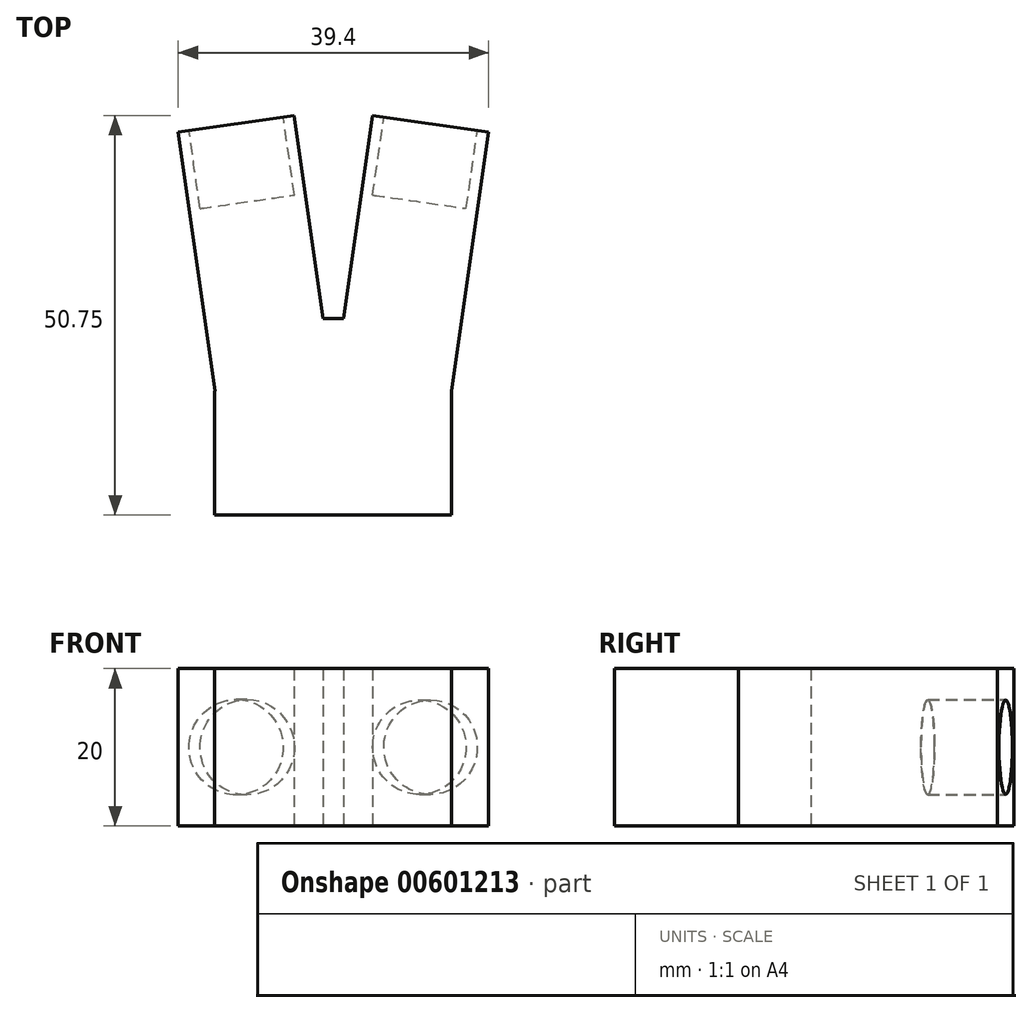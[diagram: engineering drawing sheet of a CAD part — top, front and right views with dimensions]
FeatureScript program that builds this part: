
annotation { "Feature Type Name" : "Feature", "Feature Type Description" : "" }
export const myFeature = defineFeature(function(context is Context, id is Id, definition is map)
    precondition{}
    {
        {
            var Q0;
            Q0=qCreatedBy(makeId("Top.planeOp"),FACE);
            var sketch = newSketch(context, id + "F0", { "sketchPlane" : qUnion([Q0])});
            skPoint(sketch, "E0.middle", {"position": v(0, 0) * mm});
            skLineSegment(sketch, "E1", {"start": v(-19.7, 32.9) * mm, "end": v(-15, 0) * mm});
            skLineSegment(sketch, "E2", {"start": v(19.7, 32.9) * mm, "end": v(15, 0) * mm});
            skPoint(sketch, "E3", {"position": v(-5, 35) * mm});
            skPoint(sketch, "E4", {"position": v(5, 35) * mm});
            skLineSegment(sketch, "E5", {"start": v(-1.32, 9.22) * mm, "end": v(-5, 35) * mm});
            skLineSegment(sketch, "E6", {"start": v(1.32, 9.22) * mm, "end": v(5, 35) * mm});
            skLineSegment(sketch, "E7", {"start": v(-1.32, 9.22) * mm, "end": v(1.32, 9.22) * mm});
            skPoint(sketch, "E8.start.orphan", {"position": v(16.32, 9.22) * mm});
            skPoint(sketch, "E9.orphan", {"position": v(-20, -35) * mm});
            skPoint(sketch, "E10.orphan", {"position": v(20, -35) * mm});
            skPoint(sketch, "E0.top.end.orphan", {"position": v(-10, -35) * mm});
            skPoint(sketch, "E11.orphan", {"position": v(10, -35) * mm});
            skLineSegment(sketch, "E12", {"start": v(-5, 35) * mm, "end": v(-19.7, 32.9) * mm});
            skLineSegment(sketch, "E13", {"start": v(5, 35) * mm, "end": v(20, 32.86) * mm});
            skPoint(sketch, "E14.orphan", {"position": v(-20, 35) * mm});
            skPoint(sketch, "E15.orphan", {"position": v(20, 35) * mm});
            skLineSegment(sketch, "E16.bottom", {"start": v(-15, 0) * mm, "end": v(-15.07, 0) * mm});
            skLineSegment(sketch, "E16.top", {"start": v(15, -15.75) * mm, "end": v(-15.07, -15.75) * mm});
            skLineSegment(sketch, "E16.left", {"start": v(15, 0) * mm, "end": v(15, -15.75) * mm});
            skLineSegment(sketch, "E16.right", {"start": v(-15.07, 0) * mm, "end": v(-15.07, -15.75) * mm});
            skSolve(sketch);
        }
        {
            var Q0;
            Q0 = qSketchRegion(id + "F0", true);
            extrude(context, id + "F1", {"entities" : qUnion([Q0]), "depth" : 20 * mm, "offsetDistance" : 25 * mm});
        }
        {
            var Q0;
            Q0=makeQuery(id+"F1.opExtrude","SWEPT_FACE",FACE,{"disambiguationData":[OSD([sQuery(id+"F0.wireOp",EDGE,"E12")])]});
            var sketch = newSketch(context, id + "F2", { "sketchPlane" : qUnion([Q0])});
            skCircle(sketch, "E17", {"center": v(7.42, 10) * mm, "radius": 6.05 * mm});
            skPoint(sketch, "E17.centerSnap0", {"position": v(14.85, 10) * mm});
            skPoint(sketch, "E17.centerSnap1", {"position": v(7.42, 0) * mm});
            skSolve(sketch);
        }
        {
            var Q0;
            Q0 = qSketchRegion(id + "F2", true);
            extrude(context, id + "F3", {"entities" : qUnion([Q0]), "operationType" : NewBodyOperationType.REMOVE, "oppositeDirection" : true, "depth" : 10 * mm, "offsetDistance" : 25 * mm});
        }
        {
            var Q0;
            Q0=makeQuery(id+"F1.opExtrude","SWEPT_FACE",FACE,{"disambiguationData":[OSD([sQuery(id+"F0.wireOp",EDGE,"E13")])]});
            var sketch = newSketch(context, id + "F4", { "sketchPlane" : qUnion([Q0])});
            skCircle(sketch, "E18", {"center": v(-7.42, 10) * mm, "radius": 6 * mm});
            skPoint(sketch, "E18.centerSnap0", {"position": v(-14.85, 10) * mm});
            skPoint(sketch, "E18.centerSnap1", {"position": v(-7.42, 0) * mm});
            skSolve(sketch);
        }
        {
            var Q0;
            Q0 = qSketchRegion(id + "F4", true);
            extrude(context, id + "F5", {"entities" : qUnion([Q0]), "operationType" : NewBodyOperationType.REMOVE, "oppositeDirection" : true, "depth" : 10 * mm, "offsetDistance" : 25 * mm});
        }
    });
